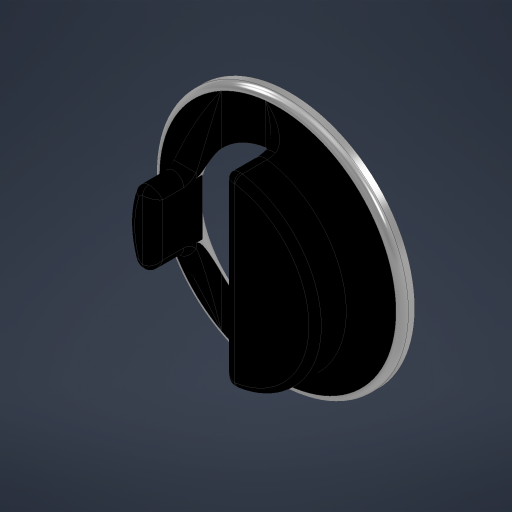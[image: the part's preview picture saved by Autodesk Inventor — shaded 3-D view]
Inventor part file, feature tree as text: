
AUTODESK INVENTOR PART (.ipt)
format: ipt  version: 2023 (Build 270158000, 158)  size: 467,456 bytes
history: native  units: mm
features: fillet x8, extrude x6, sketch x5
ambient origin geometry x8: Origin, YZ Plane, XZ Plane, XY Plane, X Axis, Y Axis, Z Axis, Center Point
bodies: Solid1 (feature_tree)
feature tree (19):
  extrude  "Extrusion1"  Depth=10.0mm TaperAngle=0.0deg
  extrude  "Extrusion2"  Depth=5.0mm TaperAngle=0.0deg
  fillet  "Fillet1"  Radius=20.0mm
  fillet  "Fillet2"  Radius=5.0mm
  fillet  "Fillet3"  Radius=5.0mm
  extrude  "Extrusion3"  Depth=45.0mm TaperAngle=0.0deg
  fillet  "Fillet4"  Radius=20.0mm
  extrude  "Extrusion4"  Depth=45.0mm
  sketch  "Sketch5"  dims[d15=30.0mm d16=0.0mm d17=30.0mm d18=0.0mm d19=35.0mm d20=0.0mm d21=10.0mm d22=5.0mm d23=10.0mm d24=8.0mm]
  extrude  "Extrusion5"  Depth=5.0mm TaperAngle=0.0deg
  extrude  "Extrusion6"  Depth=5.0mm TaperAngle=0.0deg
  fillet  "Fillet5"  Radius=10.0mm
  fillet  "Fillet6"  Radius=5.0mm
  fillet  "Fillet7"  Radius=10.0mm
  fillet  "Fillet8"  Radius=8.0mm
  sketch  "Sketch1"  dims[d0=200.0mm d1=10.0mm d2=0.0mm]
  sketch  "Sketch2"  dims[d3=150.0mm d4=45.0mm d5=0.0mm d6=20.0mm d7=5.0mm d8=5.0mm]
  sketch  "Sketch3"  dims[d9=15.0mm d10=45.0mm d11=0.0mm d12=20.0mm]
  sketch  "Sketch4"  dims[d13=22.5mm d14=45.0mm]
